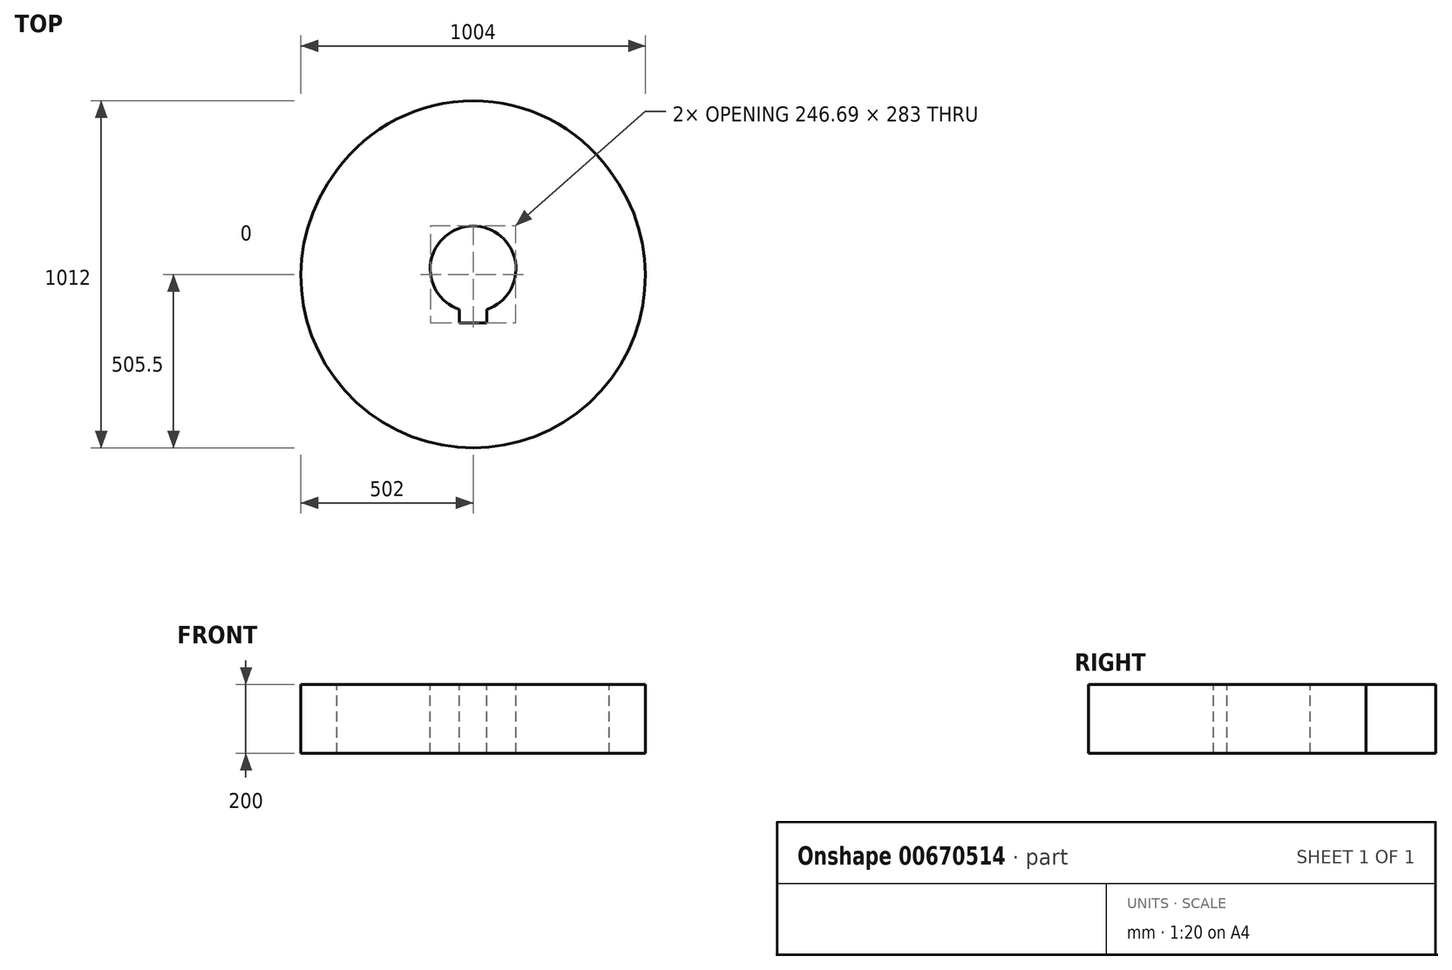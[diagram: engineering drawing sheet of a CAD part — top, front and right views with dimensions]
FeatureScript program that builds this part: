
annotation { "Feature Type Name" : "Feature", "Feature Type Description" : "" }
export const myFeature = defineFeature(function(context is Context, id is Id, definition is map)
    precondition{}
    {
        {
            var Q0;
            Q0=qCreatedBy(makeId("Top.planeOp"),FACE);
            var sketch = newSketch(context, id + "F0", { "sketchPlane" : qUnion([Q0])});
            skCircle(sketch, "E0", {"center": v(0, 0) * mm, "radius": 490 * mm});
            skCircle(sketch, "E1", {"center": v(0, -20) * mm, "radius": 502 * mm});
            skSolve(sketch);
        }
        {
            var Q0;
            Q0 = qSketchRegion(id + "F0", true);
            var Q1;
            Q1 = qSketchRegion(id + "FwsmkBZWhkTeCVy_0", true);
            extrude(context, id + "F1", {"entities" : qUnion([Q0, Q1]), "oppositeDirection" : true, "depth" : 200 * mm, "offsetDistance" : 25.4 * mm});
        }
        {
            var Q0;
            Q0=qCreatedBy(makeId("Top.planeOp"),FACE);
            var sketch = newSketch(context, id + "F2", { "sketchPlane" : qUnion([Q0])});
            skCircle(sketch, "E2", {"center": v(0, 0) * mm, "radius": 125 * mm});
            skLineSegment(sketch, "E3.bottom", {"start": v(-40, 0) * mm, "end": v(40, 0) * mm});
            skLineSegment(sketch, "E3.top", {"start": v(-40, -158) * mm, "end": v(40, -158) * mm});
            skLineSegment(sketch, "E3.left", {"start": v(-40, 0) * mm, "end": v(-40, -158) * mm});
            skLineSegment(sketch, "E3.right", {"start": v(40, 0) * mm, "end": v(40, -158) * mm});
            skSolve(sketch);
        }
        {
            var Q0;
            Q0 = qSketchRegion(id + "F2", true);
            extrude(context, id + "F3", {"entities" : qUnion([Q0]), "operationType" : NewBodyOperationType.REMOVE, "oppositeDirection" : true, "depth" : 469.9 * mm, "offsetDistance" : 25.4 * mm});
        }
    });
